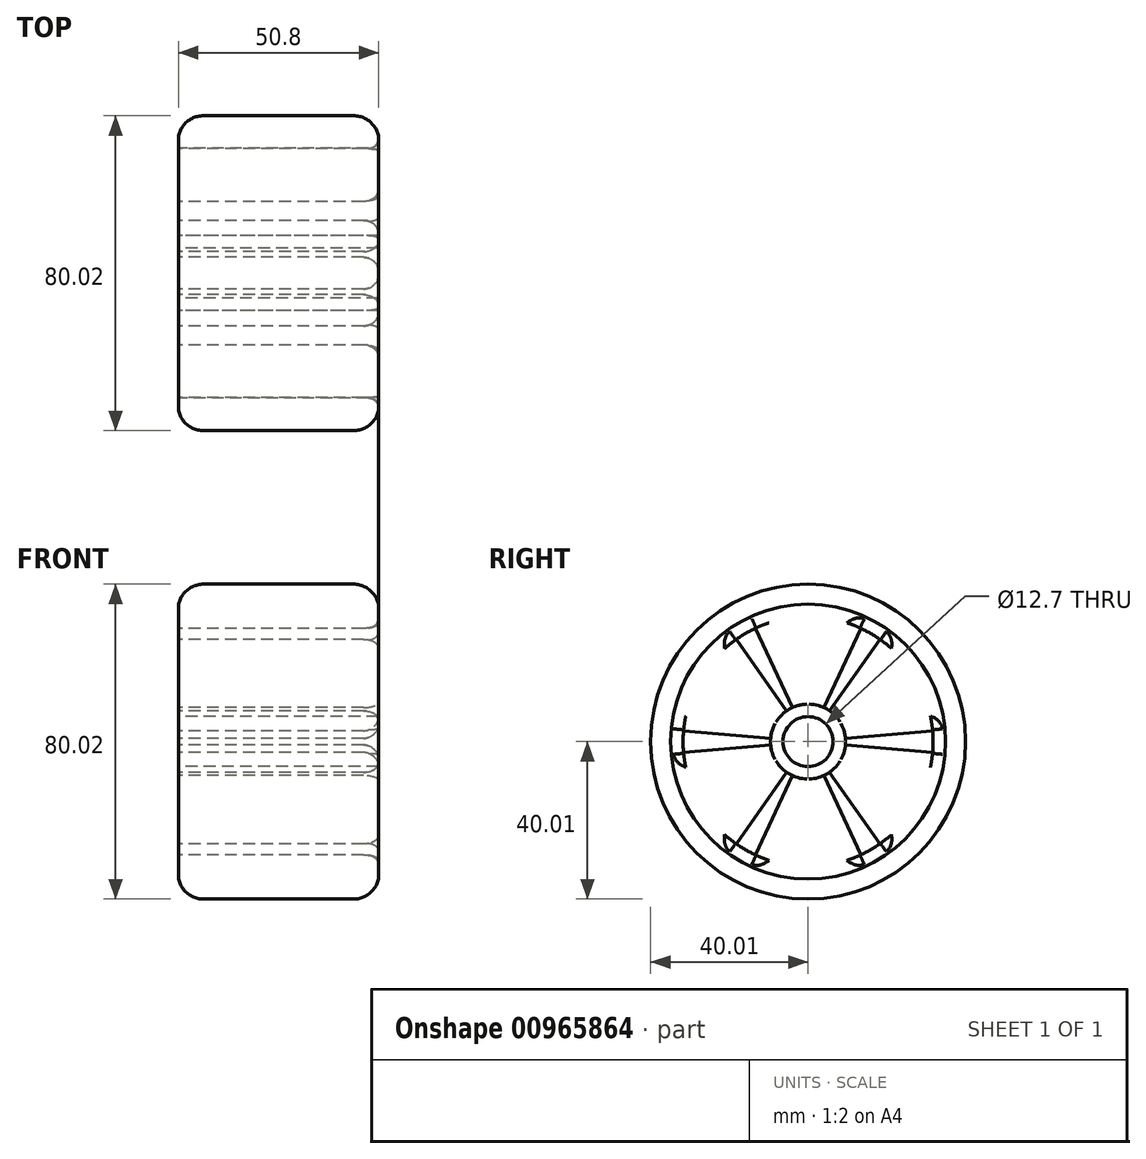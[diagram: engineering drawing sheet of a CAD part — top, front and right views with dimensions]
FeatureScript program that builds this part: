
annotation { "Feature Type Name" : "Feature", "Feature Type Description" : "" }
export const myFeature = defineFeature(function(context is Context, id is Id, definition is map)
    precondition{}
    {
        {
            var Q0;
            Q0=qCreatedBy(makeId("Right.planeOp"),FACE);
            var sketch = newSketch(context, id + "F0", { "sketchPlane" : qUnion([Q0])});
            skCircle(sketch, "E0", {"center": v(0, 0) * mm, "radius": 6.35 * mm});
            skCircle(sketch, "E1", {"center": v(0, 0) * mm, "radius": 34.93 * mm});
            skSolve(sketch);
        }
        {
            var Q0;
            Q0=makeQuery(id+"F0.imprint","IMPRINT",FACE,{"disambiguationData":[TD([[makeQuery(id+"F0.imprint","IMPRINT",EDGE,{"derivedFrom":sQuery(id+"F0.wireOp",EDGE,"E0")}),-1.0]])]});
            extrude(context, id + "F1", {"entities" : qUnion([Q0]), "depth" : 50.8 * mm, "offsetDistance" : 25.4 * mm});
        }
        {
            var Q0;
            Q0=qCreatedBy(makeId("Front.planeOp"),FACE);
            var sketch = newSketch(context, id + "F2", { "sketchPlane" : qUnion([Q0])});
            skLineSegment(sketch, "E2", {"start": v(0, 0) * mm, "end": v(9.81, 0) * mm});
            skLineSegment(sketch, "E3", {"start": v(0, 9.52) * mm, "end": v(0, 34.93) * mm});
            skLineSegment(sketch, "E4", {"start": v(0, 34.93) * mm, "end": v(6.35, 34.93) * mm});
            skLineSegment(sketch, "E5", {"start": v(6.35, 34.93) * mm, "end": v(6.35, 40) * mm});
            skLineSegment(sketch, "E6", {"start": v(6.35, 34.93) * mm, "end": v(44.45, 34.93) * mm});
            skLineSegment(sketch, "E7", {"start": v(44.45, 34.93) * mm, "end": v(44.45, 40) * mm});
            skLineSegment(sketch, "E8", {"start": v(6.35, 40) * mm, "end": v(44.45, 40) * mm});
            skLineSegment(sketch, "E9", {"start": v(44.45, 34.93) * mm, "end": v(50.8, 34.93) * mm});
            skArc(sketch, "E10", {"start": v(6.35, 40) * mm, "mid": v(2.28, 38.58) * mm, "end": v(0, 34.93) * mm});
            skArc(sketch, "E11", {"start": v(50.8, 34.92) * mm, "mid": v(48.52, 38.58) * mm, "end": v(44.45, 40) * mm});
            skLineSegment(sketch, "E12", {"start": v(0, 0) * mm, "end": v(0, 34.93) * mm});
            skLineSegment(sketch, "E13", {"start": v(0, 34.93) * mm, "end": v(23.95, 34.93) * mm});
            skSolve(sketch);
        }
        {
            var Q0;
            {var subQ1=sQuery(id+"F2.wireOp",EDGE,"E5");Q0=makeQuery(id+"F2.imprint","IMPRINT",FACE,{"disambiguationData":[TD([[makeQuery(id+"F2.imprint","IMPRINT",EDGE,{"derivedFrom":subQ1}),-1.0]])]});}
            var Q1;
            Q1=makeQuery(id+"F2.imprint","IMPRINT",FACE,{"disambiguationData":[TD([[makeQuery(id+"F2.imprint","IMPRINT",EDGE,{"derivedFrom":sQuery(id+"F2.wireOp",EDGE,"E7")}),-1.0]])]});
            var Q2;
            {var subQ0=sQuery(id+"F2.wireOp",EDGE,"E5");Q2=makeQuery(id+"F2.imprint","IMPRINT",FACE,{"disambiguationData":[TD([[makeQuery(id+"F2.imprint","IMPRINT",EDGE,{"derivedFrom":subQ0}),1.0]])]});}
            var Q3;
            Q3=sQuery(id+"F2.wireOp",EDGE,"E2");
            revolve(context, id + "F3", {"operationType" : NewBodyOperationType.ADD, "surfaceOperationType" : NewSurfaceOperationType.NEW, "entities" : qUnion([Q0, Q1, Q2]), "axis" : qUnion([Q3]), "revolveType" : RevolveType.FULL});
        }
        {
            var Q0;
            Q0=qCreatedBy(makeId("Right.planeOp"),FACE);
            var sketch = newSketch(context, id + "F4", { "sketchPlane" : qUnion([Q0])});
            skArc(sketch, "E14", {"start": v(-9.49, 0.83) * mm, "mid": v(-9.53, 0) * mm, "end": v(-9.49, -0.83) * mm});
            skArc(sketch, "E15", {"start": v(-18.21, -26) * mm, "mid": v(-15.87, -27.5) * mm, "end": v(-13.42, -28.78) * mm});
            skLineSegment(sketch, "E16", {"start": v(-9.49, 0.83) * mm, "end": v(-31.63, 2.77) * mm});
            skLineSegment(sketch, "E17", {"start": v(-5.46, 7.8) * mm, "end": v(-18.21, 26) * mm});
            skLineSegment(sketch, "E18", {"start": v(-4.03, 8.63) * mm, "end": v(-13.42, 28.78) * mm});
            skLineSegment(sketch, "E19", {"start": v(4.03, 8.63) * mm, "end": v(13.42, 28.78) * mm});
            skLineSegment(sketch, "E20", {"start": v(5.46, 7.8) * mm, "end": v(18.21, 26) * mm});
            skLineSegment(sketch, "E21", {"start": v(9.49, 0.83) * mm, "end": v(31.63, 2.77) * mm});
            skLineSegment(sketch, "E22", {"start": v(9.49, -0.83) * mm, "end": v(31.63, -2.77) * mm});
            skLineSegment(sketch, "E23", {"start": v(4.03, -8.63) * mm, "end": v(13.42, -28.78) * mm});
            skLineSegment(sketch, "E24", {"start": v(5.46, -7.8) * mm, "end": v(18.21, -26) * mm});
            skLineSegment(sketch, "E25", {"start": v(-4.03, -8.63) * mm, "end": v(-13.42, -28.78) * mm});
            skLineSegment(sketch, "E26", {"start": v(-5.46, -7.8) * mm, "end": v(-18.21, -26) * mm});
            skLineSegment(sketch, "E27", {"start": v(-9.49, -0.83) * mm, "end": v(-31.63, -2.77) * mm});
            skArc(sketch, "E28.trimOffspring", {"start": v(13.42, -28.78) * mm, "mid": v(15.88, -27.5) * mm, "end": v(18.21, -26) * mm});
            skArc(sketch, "E29.trimOffspring", {"start": v(31.63, -2.77) * mm, "mid": v(31.75, 0) * mm, "end": v(31.63, 2.77) * mm});
            skArc(sketch, "E30.trimOffspring", {"start": v(18.21, 26) * mm, "mid": v(15.87, 27.5) * mm, "end": v(13.42, 28.78) * mm});
            skArc(sketch, "E31.trimOffspring", {"start": v(-13.42, 28.78) * mm, "mid": v(-15.88, 27.5) * mm, "end": v(-18.21, 26) * mm});
            skArc(sketch, "E32.trimOffspring", {"start": v(-31.63, 2.77) * mm, "mid": v(-31.75, 0) * mm, "end": v(-31.63, -2.77) * mm});
            skArc(sketch, "E33.trimOffspring", {"start": v(-4.03, 8.63) * mm, "mid": v(-4.76, 8.25) * mm, "end": v(-5.46, 7.8) * mm});
            skArc(sketch, "E34.trimOffspring", {"start": v(5.46, 7.8) * mm, "mid": v(4.76, 8.25) * mm, "end": v(4.03, 8.63) * mm});
            skArc(sketch, "E35.trimOffspring", {"start": v(9.49, -0.83) * mm, "mid": v(9.53, 0) * mm, "end": v(9.49, 0.83) * mm});
            skArc(sketch, "E36.trimOffspring", {"start": v(4.03, -8.63) * mm, "mid": v(4.76, -8.25) * mm, "end": v(5.46, -7.8) * mm});
            skArc(sketch, "E37.trimOffspring", {"start": v(-5.46, -7.8) * mm, "mid": v(-4.76, -8.25) * mm, "end": v(-4.03, -8.63) * mm});
            skSolve(sketch);
        }
        {
            var Q0;
            Q0 = qSketchRegion(id + "F4", true);
            extrude(context, id + "F5", {"entities" : qUnion([Q0]), "operationType" : NewBodyOperationType.REMOVE, "depth" : 65.53 * mm, "offsetDistance" : 25.4 * mm});
        }
        {
            var Q0;
            Q0=makeQuery(id+"F5.boolean.opBoolean","INTERSECT",EDGE,{"derivedFrom":[makeQuery(id+"F1.opExtrude","CAP_FACE",FACE,{"disambiguationData":[OSD([sQuery(id+"F0.wireOp",EDGE,"E0"),sQuery(id+"F0.wireOp",EDGE,"E1")])],"isStart":false}),makeQuery(id+"F5.opExtrude","SWEPT_FACE",FACE,{"disambiguationData":[OSD([sQuery(id+"F4.wireOp",EDGE,"E18")])]})]});
            var Q1;
            Q1=makeQuery(id+"F5.boolean.opBoolean","INTERSECT",EDGE,{"derivedFrom":[makeQuery(id+"F1.opExtrude","CAP_FACE",FACE,{"disambiguationData":[OSD([sQuery(id+"F0.wireOp",EDGE,"E0"),sQuery(id+"F0.wireOp",EDGE,"E1")])],"isStart":false}),makeQuery(id+"F5.opExtrude","SWEPT_FACE",FACE,{"disambiguationData":[OSD([sQuery(id+"F4.wireOp",EDGE,"E17")])]})]});
            var Q2;
            Q2=makeQuery(id+"F5.boolean.opBoolean","INTERSECT",EDGE,{"derivedFrom":[makeQuery(id+"F1.opExtrude","CAP_FACE",FACE,{"disambiguationData":[OSD([sQuery(id+"F0.wireOp",EDGE,"E0"),sQuery(id+"F0.wireOp",EDGE,"E1")])],"isStart":false}),makeQuery(id+"F5.opExtrude","SWEPT_FACE",FACE,{"disambiguationData":[OSD([sQuery(id+"F4.wireOp",EDGE,"E19")])]})]});
            var Q3;
            Q3=makeQuery(id+"F5.boolean.opBoolean","INTERSECT",EDGE,{"derivedFrom":[makeQuery(id+"F1.opExtrude","CAP_FACE",FACE,{"disambiguationData":[OSD([sQuery(id+"F0.wireOp",EDGE,"E0"),sQuery(id+"F0.wireOp",EDGE,"E1")])],"isStart":false}),makeQuery(id+"F5.opExtrude","SWEPT_FACE",FACE,{"disambiguationData":[OSD([sQuery(id+"F4.wireOp",EDGE,"E20")])]})]});
            var Q4;
            Q4=makeQuery(id+"F5.boolean.opBoolean","INTERSECT",EDGE,{"derivedFrom":[makeQuery(id+"F1.opExtrude","CAP_FACE",FACE,{"disambiguationData":[OSD([sQuery(id+"F0.wireOp",EDGE,"E0"),sQuery(id+"F0.wireOp",EDGE,"E1")])],"isStart":false}),makeQuery(id+"F5.opExtrude","SWEPT_FACE",FACE,{"disambiguationData":[OSD([sQuery(id+"F4.wireOp",EDGE,"E16")])]})]});
            var Q5;
            Q5=makeQuery(id+"F5.boolean.opBoolean","INTERSECT",EDGE,{"derivedFrom":[makeQuery(id+"F1.opExtrude","CAP_FACE",FACE,{"disambiguationData":[OSD([sQuery(id+"F0.wireOp",EDGE,"E0"),sQuery(id+"F0.wireOp",EDGE,"E1")])],"isStart":false}),makeQuery(id+"F5.opExtrude","SWEPT_FACE",FACE,{"disambiguationData":[OSD([sQuery(id+"F4.wireOp",EDGE,"E27")])]})]});
            var Q6;
            Q6=makeQuery(id+"F5.boolean.opBoolean","INTERSECT",EDGE,{"derivedFrom":[makeQuery(id+"F1.opExtrude","CAP_FACE",FACE,{"disambiguationData":[OSD([sQuery(id+"F0.wireOp",EDGE,"E0"),sQuery(id+"F0.wireOp",EDGE,"E1")])],"isStart":false}),makeQuery(id+"F5.opExtrude","SWEPT_FACE",FACE,{"disambiguationData":[OSD([sQuery(id+"F4.wireOp",EDGE,"E26")])]})]});
            var Q7;
            Q7=makeQuery(id+"F5.boolean.opBoolean","INTERSECT",EDGE,{"derivedFrom":[makeQuery(id+"F1.opExtrude","CAP_FACE",FACE,{"disambiguationData":[OSD([sQuery(id+"F0.wireOp",EDGE,"E0"),sQuery(id+"F0.wireOp",EDGE,"E1")])],"isStart":false}),makeQuery(id+"F5.opExtrude","SWEPT_FACE",FACE,{"disambiguationData":[OSD([sQuery(id+"F4.wireOp",EDGE,"E25")])]})]});
            var Q8;
            Q8=makeQuery(id+"F5.boolean.opBoolean","INTERSECT",EDGE,{"derivedFrom":[makeQuery(id+"F1.opExtrude","CAP_FACE",FACE,{"disambiguationData":[OSD([sQuery(id+"F0.wireOp",EDGE,"E0"),sQuery(id+"F0.wireOp",EDGE,"E1")])],"isStart":false}),makeQuery(id+"F5.opExtrude","SWEPT_FACE",FACE,{"disambiguationData":[OSD([sQuery(id+"F4.wireOp",EDGE,"E23")])]})]});
            var Q9;
            Q9=makeQuery(id+"F5.boolean.opBoolean","INTERSECT",EDGE,{"derivedFrom":[makeQuery(id+"F1.opExtrude","CAP_FACE",FACE,{"disambiguationData":[OSD([sQuery(id+"F0.wireOp",EDGE,"E0"),sQuery(id+"F0.wireOp",EDGE,"E1")])],"isStart":false}),makeQuery(id+"F5.opExtrude","SWEPT_FACE",FACE,{"disambiguationData":[OSD([sQuery(id+"F4.wireOp",EDGE,"E24")])]})]});
            var Q10;
            Q10=makeQuery(id+"F5.boolean.opBoolean","INTERSECT",EDGE,{"derivedFrom":[makeQuery(id+"F1.opExtrude","CAP_FACE",FACE,{"disambiguationData":[OSD([sQuery(id+"F0.wireOp",EDGE,"E0"),sQuery(id+"F0.wireOp",EDGE,"E1")])],"isStart":false}),makeQuery(id+"F5.opExtrude","SWEPT_FACE",FACE,{"disambiguationData":[OSD([sQuery(id+"F4.wireOp",EDGE,"E22")])]})]});
            var Q11;
            Q11=makeQuery(id+"F5.boolean.opBoolean","INTERSECT",EDGE,{"derivedFrom":[makeQuery(id+"F1.opExtrude","CAP_FACE",FACE,{"disambiguationData":[OSD([sQuery(id+"F0.wireOp",EDGE,"E0"),sQuery(id+"F0.wireOp",EDGE,"E1")])],"isStart":false}),makeQuery(id+"F5.opExtrude","SWEPT_FACE",FACE,{"disambiguationData":[OSD([sQuery(id+"F4.wireOp",EDGE,"E21")])]})]});
            var Q12;
            Q12=makeQuery(id+"F5.boolean.opBoolean","COPY",EDGE,{"derivedFrom":makeQuery(id+"F5.opExtrude","CAP_EDGE",EDGE,{"disambiguationData":[OSD([sQuery(id+"F4.wireOp",EDGE,"E27")])],"isStart":true})});
            var Q13;
            Q13=makeQuery(id+"F5.boolean.opBoolean","COPY",EDGE,{"derivedFrom":makeQuery(id+"F5.opExtrude","CAP_EDGE",EDGE,{"disambiguationData":[OSD([sQuery(id+"F4.wireOp",EDGE,"E16")])],"isStart":true})});
            var Q14;
            Q14=makeQuery(id+"F5.boolean.opBoolean","COPY",EDGE,{"derivedFrom":makeQuery(id+"F5.opExtrude","CAP_EDGE",EDGE,{"disambiguationData":[OSD([sQuery(id+"F4.wireOp",EDGE,"E17")])],"isStart":true})});
            var Q15;
            Q15=makeQuery(id+"F5.boolean.opBoolean","COPY",EDGE,{"derivedFrom":makeQuery(id+"F5.opExtrude","CAP_EDGE",EDGE,{"disambiguationData":[OSD([sQuery(id+"F4.wireOp",EDGE,"E18")])],"isStart":true})});
            var Q16;
            Q16=makeQuery(id+"F5.boolean.opBoolean","COPY",EDGE,{"derivedFrom":makeQuery(id+"F5.opExtrude","CAP_EDGE",EDGE,{"disambiguationData":[OSD([sQuery(id+"F4.wireOp",EDGE,"E19")])],"isStart":true})});
            var Q17;
            Q17=makeQuery(id+"F5.boolean.opBoolean","COPY",EDGE,{"derivedFrom":makeQuery(id+"F5.opExtrude","CAP_EDGE",EDGE,{"disambiguationData":[OSD([sQuery(id+"F4.wireOp",EDGE,"E20")])],"isStart":true})});
            var Q18;
            Q18=makeQuery(id+"F5.boolean.opBoolean","COPY",EDGE,{"derivedFrom":makeQuery(id+"F5.opExtrude","CAP_EDGE",EDGE,{"disambiguationData":[OSD([sQuery(id+"F4.wireOp",EDGE,"E21")])],"isStart":true})});
            var Q19;
            Q19=makeQuery(id+"F5.boolean.opBoolean","COPY",EDGE,{"derivedFrom":makeQuery(id+"F5.opExtrude","CAP_EDGE",EDGE,{"disambiguationData":[OSD([sQuery(id+"F4.wireOp",EDGE,"E22")])],"isStart":true})});
            var Q20;
            Q20=makeQuery(id+"F5.boolean.opBoolean","COPY",EDGE,{"derivedFrom":makeQuery(id+"F5.opExtrude","CAP_EDGE",EDGE,{"disambiguationData":[OSD([sQuery(id+"F4.wireOp",EDGE,"E26")])],"isStart":true})});
            var Q21;
            Q21=makeQuery(id+"F5.boolean.opBoolean","COPY",EDGE,{"derivedFrom":makeQuery(id+"F5.opExtrude","CAP_EDGE",EDGE,{"disambiguationData":[OSD([sQuery(id+"F4.wireOp",EDGE,"E25")])],"isStart":true})});
            var Q22;
            Q22=makeQuery(id+"F5.boolean.opBoolean","COPY",EDGE,{"derivedFrom":makeQuery(id+"F5.opExtrude","CAP_EDGE",EDGE,{"disambiguationData":[OSD([sQuery(id+"F4.wireOp",EDGE,"E23")])],"isStart":true})});
            var Q23;
            Q23=makeQuery(id+"F5.boolean.opBoolean","COPY",EDGE,{"derivedFrom":makeQuery(id+"F5.opExtrude","CAP_EDGE",EDGE,{"disambiguationData":[OSD([sQuery(id+"F4.wireOp",EDGE,"E24")])],"isStart":true})});
            fillet(context, id + "F6", {"entities" : qUnion([Q0, Q1, Q2, Q3, Q4, Q5, Q6, Q7, Q8, Q9, Q10, Q11, Q12, Q13, Q14, Q15, Q16, Q17, Q18, Q19, Q20, Q21, Q22, Q23]), "radius" : 3.8 * mm, "tangentPropagation" : true, "allowEdgeOverflow" : false});
        }
        {
            var Q0;
            Q0=makeQuery(id+"F5.boolean.opBoolean","COPY",EDGE,{"derivedFrom":makeQuery(id+"F5.opExtrude","CAP_EDGE",EDGE,{"disambiguationData":[OSD([sQuery(id+"F4.wireOp",EDGE,"E28.trimOffspring")])],"isStart":true})});
            var Q1;
            Q1=makeQuery(id+"F5.boolean.opBoolean","COPY",EDGE,{"derivedFrom":makeQuery(id+"F5.opExtrude","CAP_EDGE",EDGE,{"disambiguationData":[OSD([sQuery(id+"F4.wireOp",EDGE,"E29.trimOffspring")])],"isStart":true})});
            var Q2;
            Q2=makeQuery(id+"F5.boolean.opBoolean","COPY",EDGE,{"derivedFrom":makeQuery(id+"F5.opExtrude","CAP_EDGE",EDGE,{"disambiguationData":[OSD([sQuery(id+"F4.wireOp",EDGE,"E30.trimOffspring")])],"isStart":true})});
            var Q3;
            Q3=makeQuery(id+"F5.boolean.opBoolean","COPY",EDGE,{"derivedFrom":makeQuery(id+"F5.opExtrude","CAP_EDGE",EDGE,{"disambiguationData":[OSD([sQuery(id+"F4.wireOp",EDGE,"E31.trimOffspring")])],"isStart":true})});
            var Q4;
            Q4=makeQuery(id+"F5.boolean.opBoolean","COPY",EDGE,{"derivedFrom":makeQuery(id+"F5.opExtrude","CAP_EDGE",EDGE,{"disambiguationData":[OSD([sQuery(id+"F4.wireOp",EDGE,"E32.trimOffspring")])],"isStart":true})});
            var Q5;
            Q5=makeQuery(id+"F5.boolean.opBoolean","COPY",EDGE,{"derivedFrom":makeQuery(id+"F5.opExtrude","CAP_EDGE",EDGE,{"disambiguationData":[OSD([sQuery(id+"F4.wireOp",EDGE,"E15")])],"isStart":true})});
            var Q6;
            Q6=makeQuery(id+"F5.boolean.opBoolean","INTERSECT",EDGE,{"derivedFrom":[makeQuery(id+"F1.opExtrude","CAP_FACE",FACE,{"disambiguationData":[OSD([sQuery(id+"F0.wireOp",EDGE,"E0"),sQuery(id+"F0.wireOp",EDGE,"E1")])],"isStart":false}),makeQuery(id+"F5.opExtrude","SWEPT_FACE",FACE,{"disambiguationData":[OSD([sQuery(id+"F4.wireOp",EDGE,"E15")])]})]});
            var Q7;
            Q7=makeQuery(id+"F5.boolean.opBoolean","INTERSECT",EDGE,{"derivedFrom":[makeQuery(id+"F1.opExtrude","CAP_FACE",FACE,{"disambiguationData":[OSD([sQuery(id+"F0.wireOp",EDGE,"E0"),sQuery(id+"F0.wireOp",EDGE,"E1")])],"isStart":false}),makeQuery(id+"F5.opExtrude","SWEPT_FACE",FACE,{"disambiguationData":[OSD([sQuery(id+"F4.wireOp",EDGE,"E28.trimOffspring")])]})]});
            var Q8;
            Q8=makeQuery(id+"F5.boolean.opBoolean","INTERSECT",EDGE,{"derivedFrom":[makeQuery(id+"F1.opExtrude","CAP_FACE",FACE,{"disambiguationData":[OSD([sQuery(id+"F0.wireOp",EDGE,"E0"),sQuery(id+"F0.wireOp",EDGE,"E1")])],"isStart":false}),makeQuery(id+"F5.opExtrude","SWEPT_FACE",FACE,{"disambiguationData":[OSD([sQuery(id+"F4.wireOp",EDGE,"E29.trimOffspring")])]})]});
            var Q9;
            Q9=makeQuery(id+"F5.boolean.opBoolean","INTERSECT",EDGE,{"derivedFrom":[makeQuery(id+"F1.opExtrude","CAP_FACE",FACE,{"disambiguationData":[OSD([sQuery(id+"F0.wireOp",EDGE,"E0"),sQuery(id+"F0.wireOp",EDGE,"E1")])],"isStart":false}),makeQuery(id+"F5.opExtrude","SWEPT_FACE",FACE,{"disambiguationData":[OSD([sQuery(id+"F4.wireOp",EDGE,"E30.trimOffspring")])]})]});
            var Q10;
            Q10=makeQuery(id+"F5.boolean.opBoolean","INTERSECT",EDGE,{"derivedFrom":[makeQuery(id+"F1.opExtrude","CAP_FACE",FACE,{"disambiguationData":[OSD([sQuery(id+"F0.wireOp",EDGE,"E0"),sQuery(id+"F0.wireOp",EDGE,"E1")])],"isStart":false}),makeQuery(id+"F5.opExtrude","SWEPT_FACE",FACE,{"disambiguationData":[OSD([sQuery(id+"F4.wireOp",EDGE,"E31.trimOffspring")])]})]});
            var Q11;
            Q11=makeQuery(id+"F5.boolean.opBoolean","INTERSECT",EDGE,{"derivedFrom":[makeQuery(id+"F1.opExtrude","CAP_FACE",FACE,{"disambiguationData":[OSD([sQuery(id+"F0.wireOp",EDGE,"E0"),sQuery(id+"F0.wireOp",EDGE,"E1")])],"isStart":false}),makeQuery(id+"F5.opExtrude","SWEPT_FACE",FACE,{"disambiguationData":[OSD([sQuery(id+"F4.wireOp",EDGE,"E32.trimOffspring")])]})]});
            fillet(context, id + "F7", {"entities" : qUnion([Q0, Q1, Q2, Q3, Q4, Q5, Q6, Q7, Q8, Q9, Q10, Q11]), "radius" : 2.54 * mm, "tangentPropagation" : true, "allowEdgeOverflow" : false});
        }
    });
